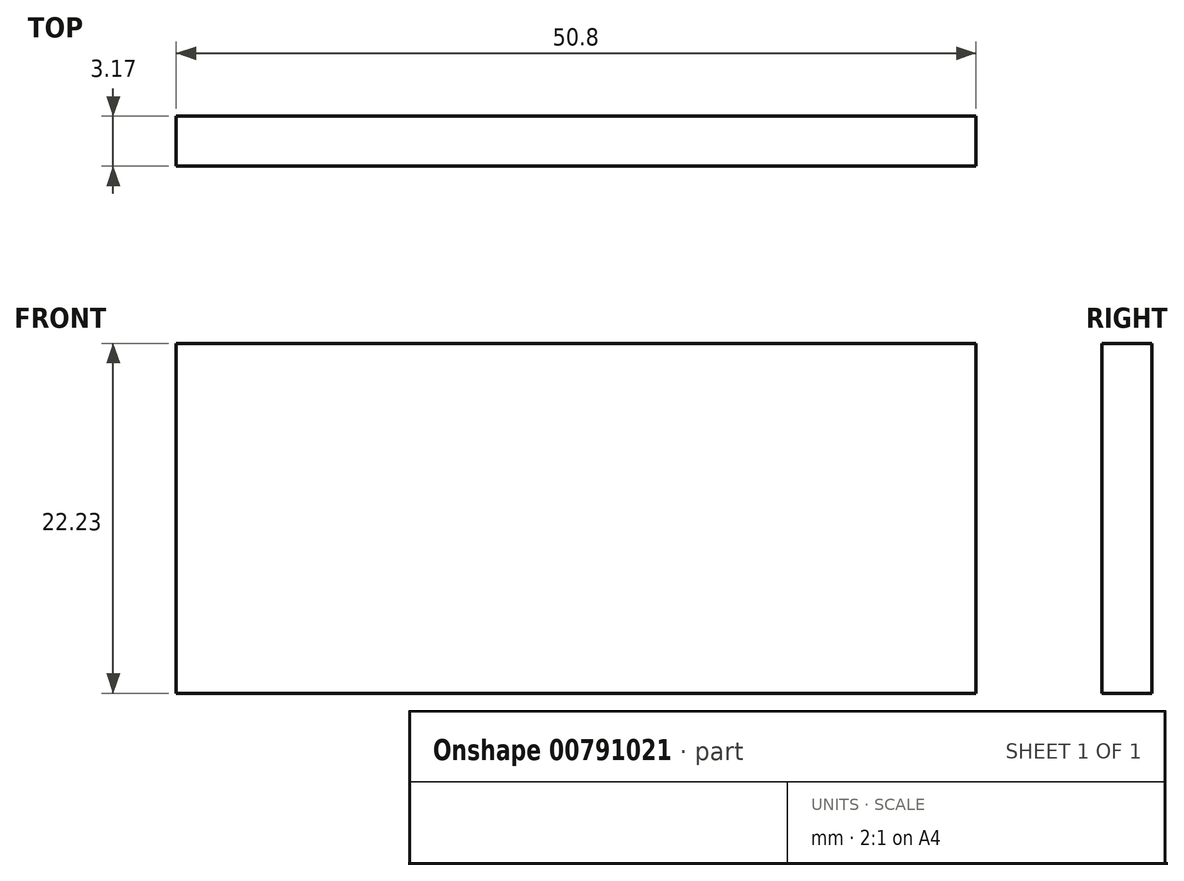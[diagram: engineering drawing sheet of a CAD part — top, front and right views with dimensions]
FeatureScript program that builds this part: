
annotation { "Feature Type Name" : "Feature", "Feature Type Description" : "" }
export const myFeature = defineFeature(function(context is Context, id is Id, definition is map)
    precondition{}
    {
        {
            var Q0;
            Q0=qCreatedBy(makeId("Front.planeOp"),FACE);
            var sketch = newSketch(context, id + "F0", { "sketchPlane" : qUnion([Q0])});
            skLineSegment(sketch, "E0.bottom", {"start": v(-30.52, -1.77) * mm, "end": v(20.28, -1.77) * mm});
            skLineSegment(sketch, "E0.top", {"start": v(-30.52, -24) * mm, "end": v(20.28, -24) * mm});
            skLineSegment(sketch, "E0.left", {"start": v(-30.52, -1.77) * mm, "end": v(-30.52, -24) * mm});
            skLineSegment(sketch, "E0.right", {"start": v(20.28, -1.77) * mm, "end": v(20.28, -24) * mm});
            skSolve(sketch);
        }
        {
            var Q0;
            Q0 = qSketchRegion(id + "F0", true);
            extrude(context, id + "F1", {"entities" : qUnion([Q0]), "depth" : 3.17 * mm, "offsetDistance" : 25.4 * mm});
        }
    });
